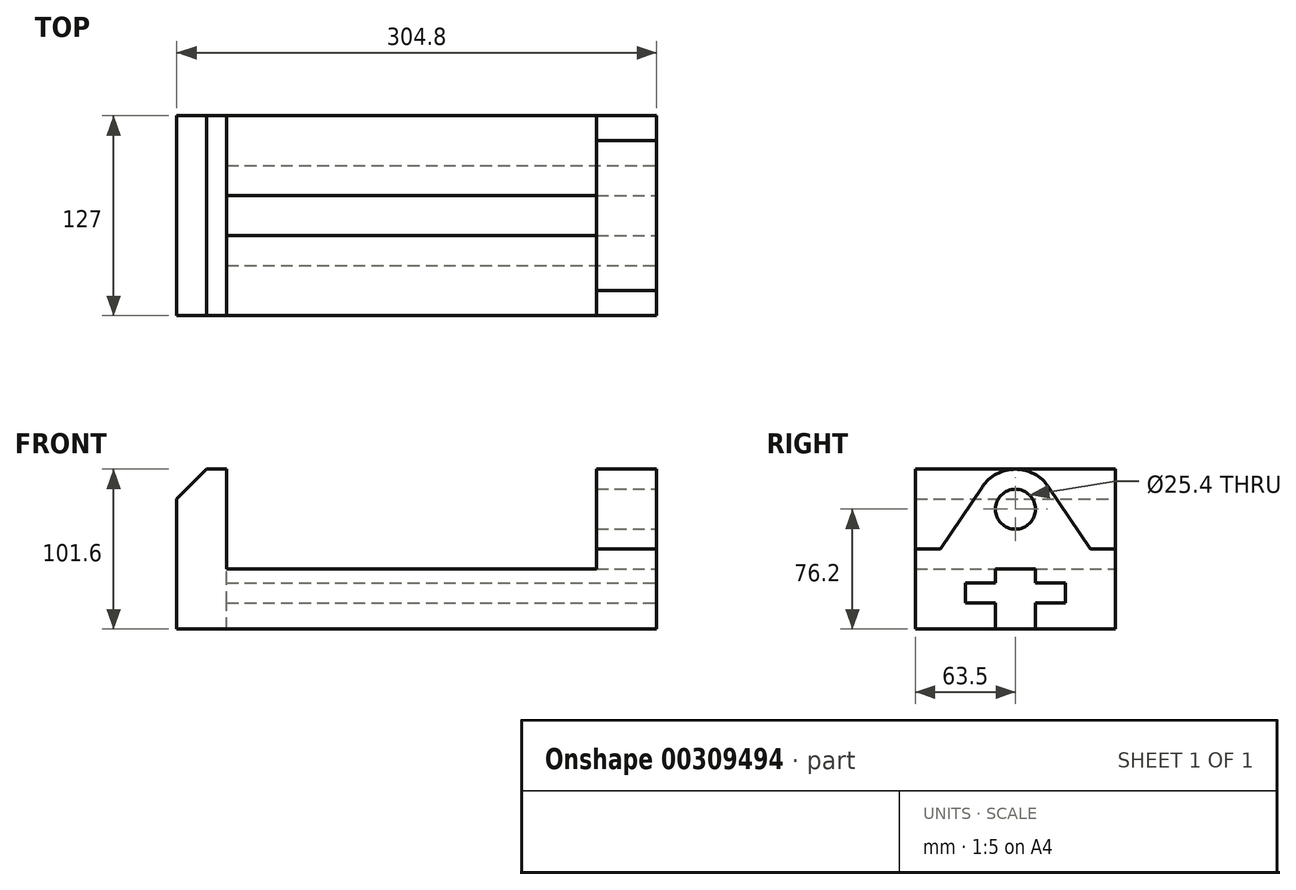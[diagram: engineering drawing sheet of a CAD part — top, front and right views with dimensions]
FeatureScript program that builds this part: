
annotation { "Feature Type Name" : "Feature", "Feature Type Description" : "" }
export const myFeature = defineFeature(function(context is Context, id is Id, definition is map)
    precondition{}
    {
        {
            var Q0;
            Q0=qCreatedBy(makeId("Front.planeOp"),FACE);
            var sketch = newSketch(context, id + "F0", { "sketchPlane" : qUnion([Q0])});
            skLineSegment(sketch, "E0", {"start": v(-304.8, 0) * mm, "end": v(0, 0) * mm});
            skLineSegment(sketch, "E1", {"start": v(0, 0) * mm, "end": v(0, 50.8) * mm});
            skLineSegment(sketch, "E2", {"start": v(0, 50.8) * mm, "end": v(-38.1, 50.8) * mm});
            skLineSegment(sketch, "E3", {"start": v(-38.1, 50.8) * mm, "end": v(-38.1, 38.1) * mm});
            skLineSegment(sketch, "E4", {"start": v(-38.1, 38.1) * mm, "end": v(-273.05, 38.1) * mm});
            skLineSegment(sketch, "E5", {"start": v(-273.05, 38.1) * mm, "end": v(-273.05, 101.6) * mm});
            skLineSegment(sketch, "E6", {"start": v(-304.8, 82.55) * mm, "end": v(-304.8, 0) * mm});
            skLineSegment(sketch, "E7", {"start": v(0, 50.8) * mm, "end": v(0, 101.6) * mm});
            skLineSegment(sketch, "E8", {"start": v(0, 101.6) * mm, "end": v(-38.1, 101.6) * mm});
            skLineSegment(sketch, "E9", {"start": v(-38.1, 101.6) * mm, "end": v(-38.1, 50.8) * mm});
            skLineSegment(sketch, "E10", {"start": v(-273.05, 101.6) * mm, "end": v(-285.75, 101.6) * mm});
            skLineSegment(sketch, "E11", {"start": v(-285.75, 101.6) * mm, "end": v(-304.8, 82.55) * mm});
            skLineSegment(sketch, "E12", {"start": v(-304.8, 82.55) * mm, "end": v(-304.8, 101.6) * mm});
            skLineSegment(sketch, "E13", {"start": v(-304.8, 101.6) * mm, "end": v(-285.75, 101.6) * mm});
            skSolve(sketch);
        }
        {
            var Q0;
            Q0 = qSketchRegion(id + "F0", true);
            extrude(context, id + "F1", {"entities" : qUnion([Q0]), "depth" : 127 * mm});
        }
        {
            var Q0;
            Q0=makeQuery(id+"F1.opExtrude","SWEPT_FACE",FACE,{"disambiguationData":[OSD([sQuery(id+"F0.wireOp",EDGE,"E1"),sQuery(id+"F0.wireOp",EDGE,"E7")])]});
            var sketch = newSketch(context, id + "F2", { "sketchPlane" : qUnion([Q0])});
            skLineSegment(sketch, "E14", {"start": v(-127, 50.8) * mm, "end": v(-111.13, 50.8) * mm});
            skLineSegment(sketch, "E15", {"start": v(-15.87, 50.8) * mm, "end": v(0, 50.8) * mm});
            skLineSegment(sketch, "E16", {"start": v(-76.2, 0) * mm, "end": v(-76.2, 16.51) * mm});
            skLineSegment(sketch, "E17", {"start": v(-76.2, 16.51) * mm, "end": v(-95.25, 16.51) * mm});
            skLineSegment(sketch, "E18", {"start": v(-95.25, 16.51) * mm, "end": v(-95.25, 29.21) * mm});
            skLineSegment(sketch, "E19", {"start": v(-95.25, 29.2) * mm, "end": v(-76.2, 29.2) * mm});
            skLineSegment(sketch, "E20", {"start": v(-76.2, 29.21) * mm, "end": v(-76.2, 38.1) * mm});
            skLineSegment(sketch, "E21", {"start": v(-76.2, 38.1) * mm, "end": v(-50.8, 38.1) * mm});
            skLineSegment(sketch, "E22", {"start": v(-50.8, 38.1) * mm, "end": v(-50.8, 29.21) * mm});
            skLineSegment(sketch, "E23", {"start": v(-50.8, 29.2) * mm, "end": v(-31.75, 29.21) * mm});
            skLineSegment(sketch, "E24", {"start": v(-31.75, 29.21) * mm, "end": v(-31.75, 16.51) * mm});
            skLineSegment(sketch, "E25", {"start": v(-31.75, 16.51) * mm, "end": v(-50.8, 16.51) * mm});
            skLineSegment(sketch, "E26", {"start": v(-50.8, 16.51) * mm, "end": v(-50.8, 0) * mm});
            skLineSegment(sketch, "E27", {"start": v(-111.13, 50.8) * mm, "end": v(-84.6, 90.35) * mm});
            skLineSegment(sketch, "E28", {"start": v(-15.87, 50.8) * mm, "end": v(-42.4, 90.35) * mm});
            skArc(sketch, "E29", {"start": v(-63.5, 101.6) * mm, "mid": v(-75.45, 98.61) * mm, "end": v(-84.6, 90.35) * mm});
            skArc(sketch, "E30", {"start": v(-42.4, 90.35) * mm, "mid": v(-51.55, 98.61) * mm, "end": v(-63.5, 101.6) * mm});
            skCircle(sketch, "E31", {"center": v(-63.5, 76.2) * mm, "radius": 12.7 * mm});
            skSolve(sketch);
        }
        {
            var Q0;
            {var subQ5=sQuery(id+"F2.wireOp",EDGE,"E14");Q0=makeQuery(id+"F2.imprint","IMPRINT",FACE,{"disambiguationData":[TD([[makeQuery(id+"F2.imprint","IMPRINT",EDGE,{"derivedFrom":subQ5}),1.0]])]});}
            var Q1;
            {var subQ5=sQuery(id+"F2.wireOp",EDGE,"E15");Q1=makeQuery(id+"F2.imprint","IMPRINT",FACE,{"disambiguationData":[TD([[makeQuery(id+"F2.imprint","IMPRINT",EDGE,{"derivedFrom":subQ5}),1.0]])]});}
            extrude(context, id + "F3", {"entities" : qUnion([Q0, Q1]), "operationType" : NewBodyOperationType.REMOVE, "oppositeDirection" : true, "depth" : 273.05 * mm});
        }
        {
            var Q0;
            Q0=makeQuery(id+"F2.imprint","IMPRINT",FACE,{"disambiguationData":[TD([[makeQuery(id+"F2.imprint","IMPRINT",EDGE,{"derivedFrom":sQuery(id+"F2.wireOp",EDGE,"E31")}),1.0]])]});
            extrude(context, id + "F4", {"entities" : qUnion([Q0]), "operationType" : NewBodyOperationType.REMOVE, "oppositeDirection" : true, "depth" : 273.05 * mm});
        }
        {
            var Q0;
            {var subQ0=sQuery(id+"F2.wireOp",EDGE,"E16");Q0=makeQuery(id+"F2.imprint","IMPRINT",FACE,{"disambiguationData":[TD([[makeQuery(id+"F2.imprint","IMPRINT",EDGE,{"derivedFrom":subQ0}),-1.0]])]});}
            extrude(context, id + "F5", {"entities" : qUnion([Q0]), "operationType" : NewBodyOperationType.REMOVE, "oppositeDirection" : true, "depth" : 273.05 * mm});
        }
        {
            var Q0;
            Q0=makeQuery(id+"F0.imprint","IMPRINT",FACE,{"disambiguationData":[TD([[makeQuery(id+"F0.imprint","IMPRINT",EDGE,{"derivedFrom":sQuery(id+"F0.wireOp",EDGE,"E11")}),-1.0]])]});
            extrude(context, id + "F6", {"entities" : qUnion([Q0]), "operationType" : NewBodyOperationType.REMOVE, "depth" : 127 * mm});
        }
    });
